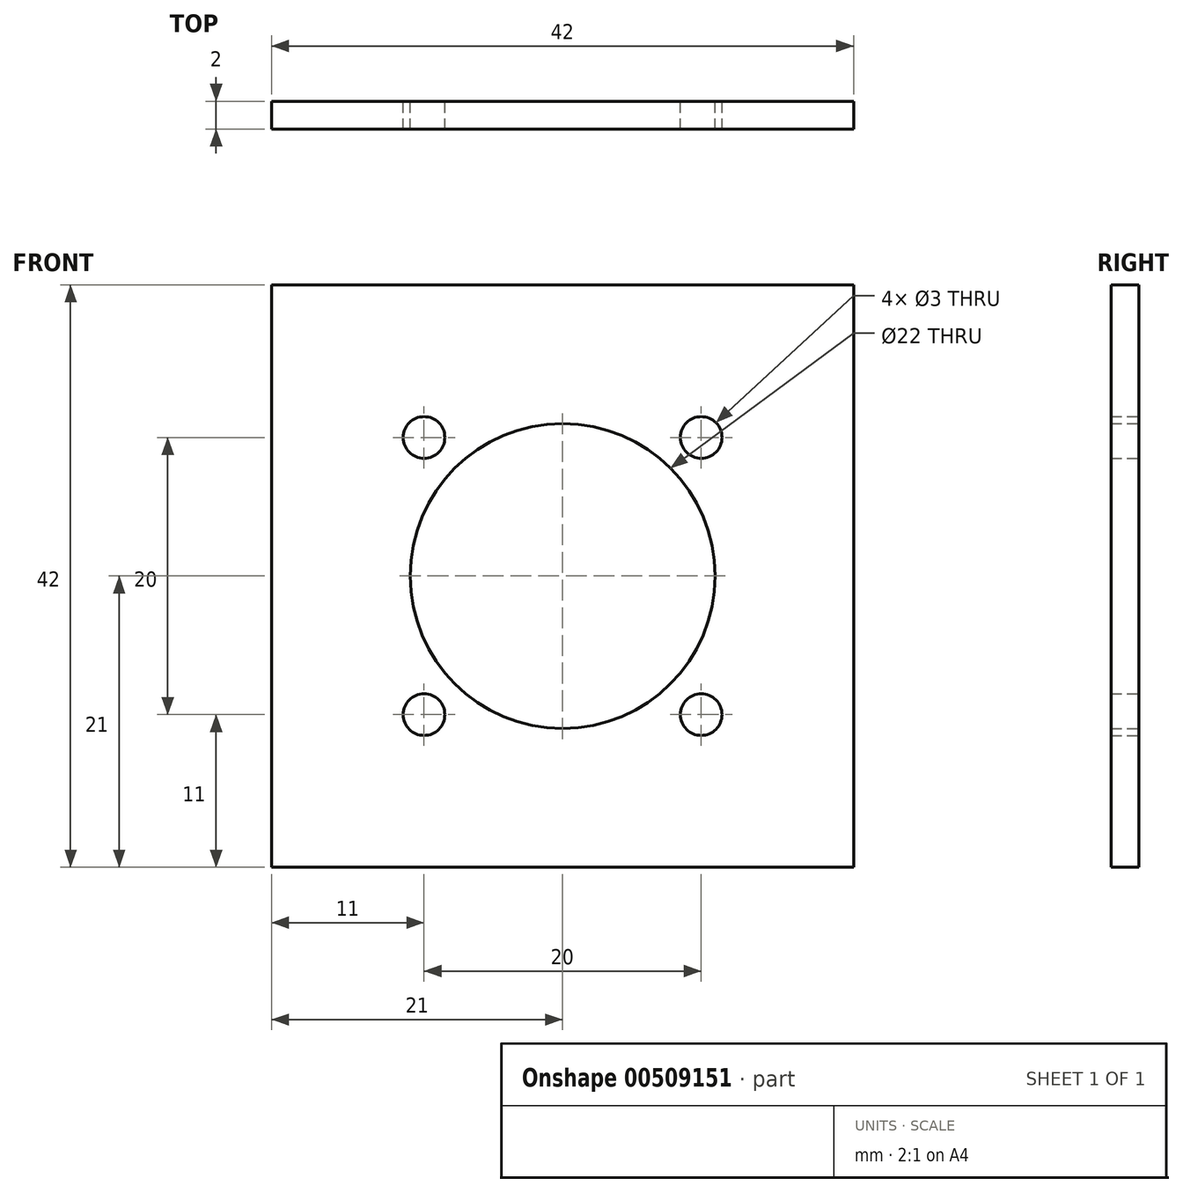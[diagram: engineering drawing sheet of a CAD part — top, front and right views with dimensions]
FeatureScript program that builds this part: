
annotation { "Feature Type Name" : "Feature", "Feature Type Description" : "" }
export const myFeature = defineFeature(function(context is Context, id is Id, definition is map)
    precondition{}
    {
        {
            var Q0;
            Q0=qCreatedBy(makeId("Front.planeOp"),FACE);
            var sketch = newSketch(context, id + "F0", { "sketchPlane" : qUnion([Q0])});
            skLineSegment(sketch, "E0.bottom", {"start": v(21, 21) * mm, "end": v(-21, 21) * mm});
            skLineSegment(sketch, "E0.top", {"start": v(21, -21) * mm, "end": v(-21, -21) * mm});
            skLineSegment(sketch, "E0.left", {"start": v(21, 21) * mm, "end": v(21, -21) * mm});
            skLineSegment(sketch, "E0.right", {"start": v(-21, 21) * mm, "end": v(-21, -21) * mm});
            skPoint(sketch, "E0.middle", {"position": v(0, 0) * mm});
            skLineSegment(sketch, "E1.bottom", {"start": v(-10, 10) * mm, "end": v(10, 10) * mm});
            skLineSegment(sketch, "E1.top", {"start": v(-10, -10) * mm, "end": v(10, -10) * mm});
            skLineSegment(sketch, "E1.left", {"start": v(-10, 10) * mm, "end": v(-10, -10) * mm});
            skLineSegment(sketch, "E1.right", {"start": v(10, 10) * mm, "end": v(10, -10) * mm});
            skCircle(sketch, "E2", {"center": v(-10, 10) * mm, "radius": 1.5 * mm});
            skCircle(sketch, "E3", {"center": v(10, 10) * mm, "radius": 1.5 * mm});
            skCircle(sketch, "E4", {"center": v(10, -10) * mm, "radius": 1.5 * mm});
            skCircle(sketch, "E5", {"center": v(-10, -10) * mm, "radius": 1.5 * mm});
            skCircle(sketch, "E6", {"center": v(0, 0) * mm, "radius": 11 * mm});
            skSolve(sketch);
        }
        {
            var Q0;
            Q0 = qSketchRegion(id + "F0", true);
            var Q1;
            {var subQ0=sQuery(id+"F0.wireOp",EDGE,"E2");var subQ1=sQuery(id+"F0.wireOp",EDGE,"E1.bottom");var subQ2=makeQuery(id+"F0.imprint","INTERSECT",VERTEX,{"derivedFrom":[subQ1,subQ0]});Q1=makeQuery(id+"F0.imprint","IMPRINT",FACE,{"disambiguationData":[TD([[makeQuery(id+"F0.imprint","IMPRINT",EDGE,{"disambiguationData":[TD([[subQ2,-1.0]])],"derivedFrom":subQ1}),-1.0]])]});}
            var Q2;
            {var subQ0=sQuery(id+"F0.wireOp",EDGE,"E5");var subQ1=sQuery(id+"F0.wireOp",EDGE,"E1.top");var subQ2=makeQuery(id+"F0.imprint","INTERSECT",VERTEX,{"derivedFrom":[subQ1,subQ0]});Q2=makeQuery(id+"F0.imprint","IMPRINT",FACE,{"disambiguationData":[TD([[makeQuery(id+"F0.imprint","IMPRINT",EDGE,{"disambiguationData":[TD([[subQ2,-1.0]])],"derivedFrom":subQ1}),1.0]])]});}
            var Q3;
            {var subQ0=sQuery(id+"F0.wireOp",EDGE,"E6");var subQ1=sQuery(id+"F0.wireOp",EDGE,"E1.top");var subQ2=makeQuery(id+"F0.imprint","INTERSECT",VERTEX,{"disambiguationData":[OD(1.0)],"derivedFrom":[subQ1,subQ0]});Q3=makeQuery(id+"F0.imprint","IMPRINT",FACE,{"disambiguationData":[TD([[makeQuery(id+"F0.imprint","IMPRINT",EDGE,{"disambiguationData":[TD([[subQ2,-1.0]])],"derivedFrom":subQ1}),1.0]])]});}
            var Q4;
            {var subQ0=sQuery(id+"F0.wireOp",EDGE,"E6");var subQ1=sQuery(id+"F0.wireOp",EDGE,"E1.bottom");var subQ2=makeQuery(id+"F0.imprint","INTERSECT",VERTEX,{"disambiguationData":[OD(1.0)],"derivedFrom":[subQ1,subQ0]});Q4=makeQuery(id+"F0.imprint","IMPRINT",FACE,{"disambiguationData":[TD([[makeQuery(id+"F0.imprint","IMPRINT",EDGE,{"disambiguationData":[TD([[subQ2,-1.0]])],"derivedFrom":subQ1}),-1.0]])]});}
            extrude(context, id + "F1", {"entities" : qUnion([Q0, Q1, Q2, Q3, Q4]), "depth" : 2 * mm, "offsetDistance" : 25 * mm});
        }
    });
